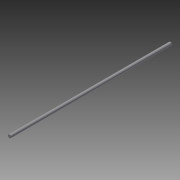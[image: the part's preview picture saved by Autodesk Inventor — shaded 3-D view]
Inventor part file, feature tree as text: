
AUTODESK INVENTOR PART (.ipt)
format: ipt  version: 2015 (Build 190159000, 159)  size: 65,536 bytes
history: native  units: in
note: dims shown in document units (in); Inventor stores cm internally (conversion verified against a paired STEP export)
features: extrude x1, sketch x1
ambient origin geometry x8: Origin, YZ Plane, XZ Plane, XY Plane, X Axis, Y Axis, Z Axis, Center Point
bodies: Solid1 (feature_tree)
feature tree (2):
  extrude  "Extrusion1"  Depth=13.0in TaperAngle=0.0deg
  sketch  "Sketch1"  dims[d0=0.25in d1=13.0in d2=0.0in]
